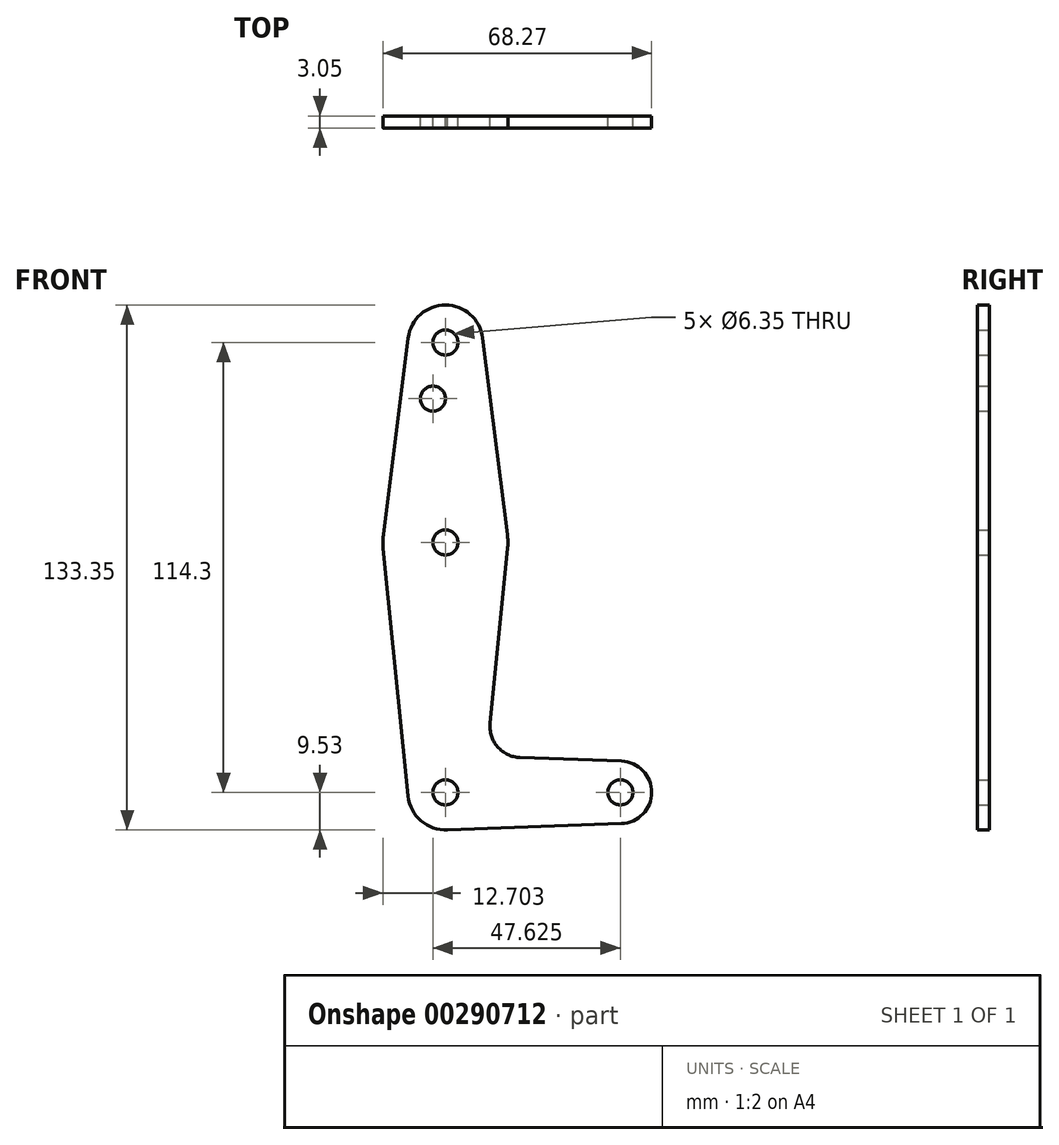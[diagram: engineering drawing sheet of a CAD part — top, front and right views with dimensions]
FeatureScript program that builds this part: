
annotation { "Feature Type Name" : "Feature", "Feature Type Description" : "" }
export const myFeature = defineFeature(function(context is Context, id is Id, definition is map)
    precondition{}
    {
        {
            var Q0;
            Q0=qCreatedBy(makeId("Front.planeOp"),FACE);
            var sketch = newSketch(context, id + "F0", { "sketchPlane" : qUnion([Q0])});
            skCircle(sketch, "E0", {"center": v(-58.33, 50.8) * mm, "radius": 9.53 * mm});
            skCircle(sketch, "E1", {"center": v(-58.33, 0) * mm, "radius": 15.88 * mm});
            skCircle(sketch, "E2", {"center": v(-58.33, -63.5) * mm, "radius": 9.53 * mm});
            skCircle(sketch, "E3", {"center": v(-13.88, -63.5) * mm, "radius": 7.94 * mm});
            skLineSegment(sketch, "E4", {"start": v(-58.33, 50.8) * mm, "end": v(-58.33, 0) * mm});
            skLineSegment(sketch, "E5", {"start": v(-58.33, 0) * mm, "end": v(-58.33, -63.5) * mm});
            skLineSegment(sketch, "E6", {"start": v(-58.33, -63.5) * mm, "end": v(-13.88, -63.5) * mm});
            skLineSegment(sketch, "E7", {"start": v(-74.13, -1.59) * mm, "end": v(-67.8, -64.45) * mm});
            skLineSegment(sketch, "E8", {"start": v(-42.54, -1.59) * mm, "end": v(-47, -45.91) * mm});
            skLineSegment(sketch, "E9", {"start": v(-39.36, -54.65) * mm, "end": v(-13.6, -55.57) * mm});
            skLineSegment(sketch, "E10", {"start": v(-57.78, -73) * mm, "end": v(-13.6, -71.43) * mm});
            skCircle(sketch, "E11", {"center": v(-61.5, 36.53) * mm, "radius": 3.18 * mm});
            skCircle(sketch, "E12", {"center": v(-58.33, 50.8) * mm, "radius": 3.18 * mm});
            skCircle(sketch, "E13", {"center": v(-58.33, 0) * mm, "radius": 3.18 * mm});
            skCircle(sketch, "E14", {"center": v(-58.33, -63.5) * mm, "radius": 3.18 * mm});
            skCircle(sketch, "E15", {"center": v(-13.88, -63.5) * mm, "radius": 3.18 * mm});
            skArc(sketch, "E16.filletArc", {"start": v(-47, -45.91) * mm, "mid": v(-45.07, -51.93) * mm, "end": v(-39.36, -54.65) * mm});
            skLineSegment(sketch, "E17", {"start": v(-67.78, 52) * mm, "end": v(-74.08, 1.98) * mm});
            skLineSegment(sketch, "E18", {"start": v(-48.88, 52) * mm, "end": v(-42.58, 1.98) * mm});
            skSolve(sketch);
        }
        {
            var Q0;
            Q0 = qSketchRegion(id + "F0", true);
            var Q1;
            {var subQ0=sQuery(id+"F0.wireOp",EDGE,"E5");var subQ1=sQuery(id+"F0.wireOp",EDGE,"E2");var subQ2=makeQuery(id+"F0.imprint","INTERSECT",VERTEX,{"derivedFrom":[subQ1,subQ0]});Q1=makeQuery(id+"F0.imprint","IMPRINT",FACE,{"disambiguationData":[TD([[makeQuery(id+"F0.imprint","IMPRINT",EDGE,{"disambiguationData":[TD([[subQ2,1.0]])],"derivedFrom":subQ1}),1.0]])]});}
            extrude(context, id + "F1", {"entities" : qUnion([Q0, Q1]), "depth" : 3.05 * mm});
        }
    });
